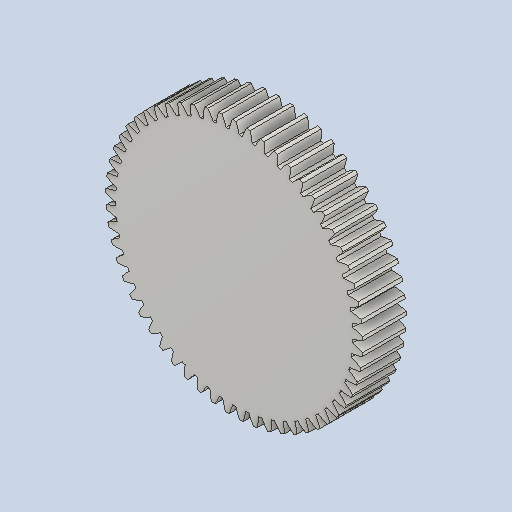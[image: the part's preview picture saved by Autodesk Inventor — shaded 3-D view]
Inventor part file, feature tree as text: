
AUTODESK INVENTOR PART (.ipt)
format: ipt  version: 2023.2 (Build 272271000, 271)  size: 375,808 bytes
history: native  units: mm (DEFAULTED — no unit token found)
features: plane x3, other x3, sketch x2, extrude x1
ambient origin geometry x8: Origin, YZ Plane, XZ Plane, XY Plane, X Axis, Y Axis, Z Axis, Center Point
bodies: Solid1 (feature_tree)
feature tree (9):
  extrude  "Extrusion1"  Depth=20.0mm TaperAngle=0.0deg
  plane  "Work Plane2"
  plane  "Work Plane8"
  plane  "Work Plane9"
  other  "Spur Gear"
  sketch  "Sketch1"  dims[d0=118.0mm d1=20.0mm d2=0.0mm]
  sketch  "Sketch2"  dims[d3=114.0mm d4=10.0mm d5=0.0mm d16=80.0mm d17=0.0mm d34=0.551157mm d39=0.0mm d41=0.0mm d43=80.0mm d46=80.0mm d47=0.0mm d48=0.0mm]
  other  "Srf1"
  other  "Pitch Diameter"
